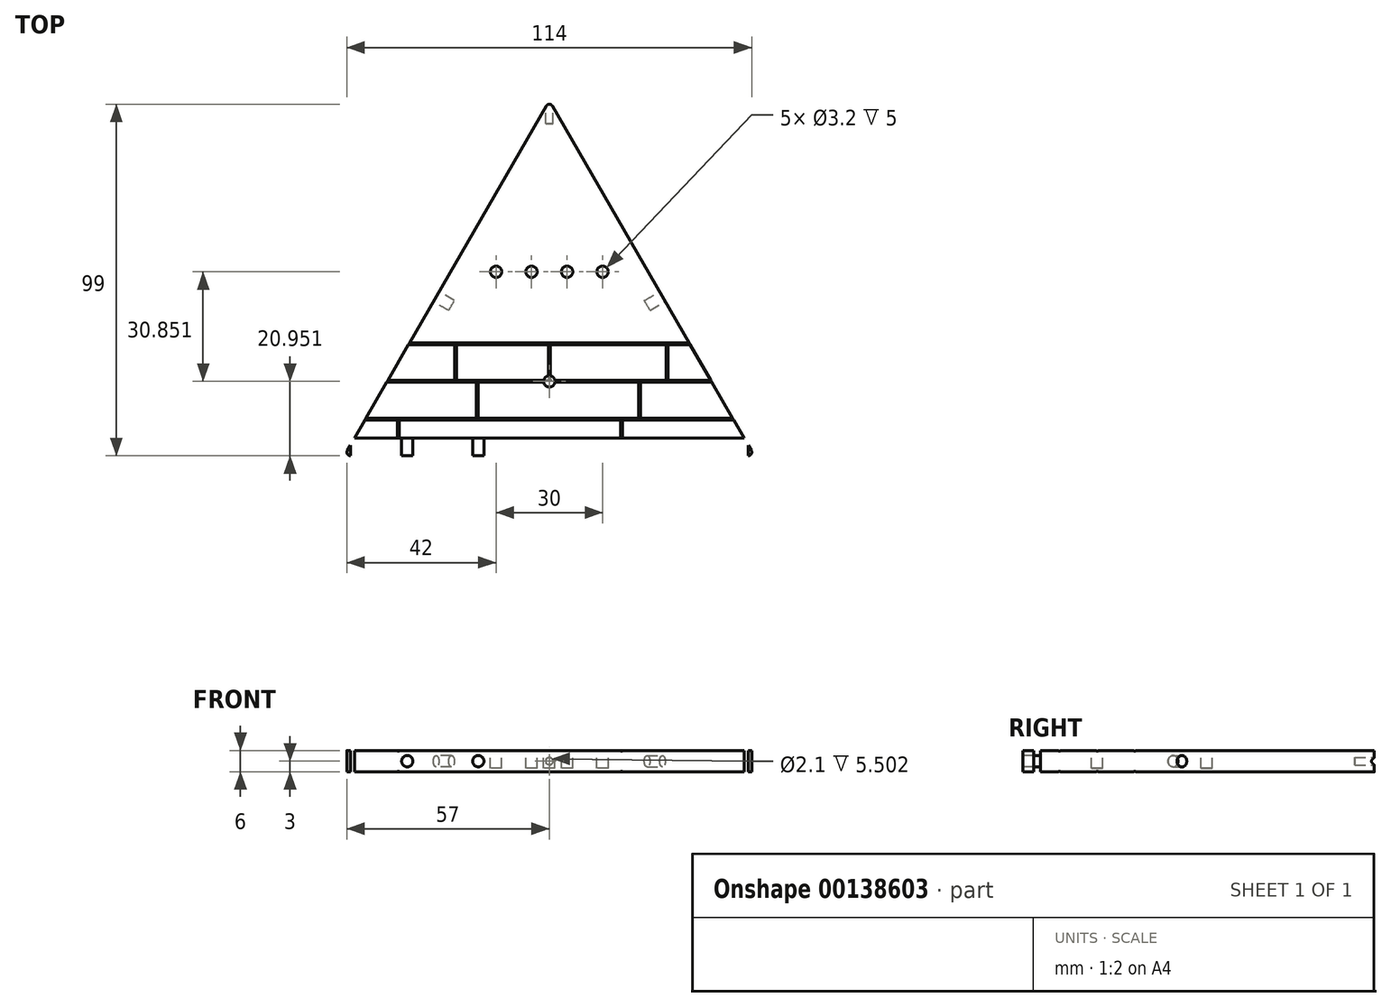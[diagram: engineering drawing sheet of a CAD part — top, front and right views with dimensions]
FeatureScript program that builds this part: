
annotation { "Feature Type Name" : "Feature", "Feature Type Description" : "" }
export const myFeature = defineFeature(function(context is Context, id is Id, definition is map)
    precondition{}
    {
        {
            assignVariable(context, id + "F0", {"name" : "mortar_depth", "anyValue" : 0.15 * mm});
        }
        {
            assignVariable(context, id + "F1", {"name" : "pinhole_depth", "anyValue" : 5 * mm});
        }
        {
            var Q0;
            Q0=qCreatedBy(makeId("Top.planeOp"),FACE);
            var sketch = newSketch(context, id + "F2", { "sketchPlane" : qUnion([Q0])});
            skLineSegment(sketch, "E0", {"start": v(-0.87, 98.5) * mm, "end": v(-56.87, 1.5) * mm});
            skLineSegment(sketch, "E1", {"start": v(-56, 0) * mm, "end": v(56, 0) * mm});
            skLineSegment(sketch, "E2", {"start": v(56.87, 1.5) * mm, "end": v(0.87, 98.5) * mm});
            skPoint(sketch, "E3.visualSharp", {"position": v(0, 100) * mm});
            skArc(sketch, "E3.filletArc", {"start": v(0.87, 98.5) * mm, "mid": v(0, 99) * mm, "end": v(-0.87, 98.5) * mm});
            skPoint(sketch, "E4.visualSharp", {"position": v(-57.74, 0) * mm});
            skArc(sketch, "E4.filletArc", {"start": v(-56.87, 1.5) * mm, "mid": v(-56.87, 0.5) * mm, "end": v(-56, 0) * mm});
            skPoint(sketch, "E5.visualSharp", {"position": v(57.74, 0) * mm});
            skArc(sketch, "E5.filletArc", {"start": v(56, 0) * mm, "mid": v(56.87, 0.5) * mm, "end": v(56.87, 1.5) * mm});
            skLineSegment(sketch, "E6", {"start": v(0, 100) * mm, "end": v(0, 0) * mm, "construction": true});
            skSolve(sketch);
        }
        {
            var Q0;
            Q0=makeQuery(id+"F2.imprint","IMPRINT",FACE,{"disambiguationData":[TD([[makeQuery(id+"F2.imprint","IMPRINT",EDGE,{"derivedFrom":sQuery(id+"F2.wireOp",EDGE,"E0")}),1.0]])]});
            extrude(context, id + "F3", {"entities" : qUnion([Q0]), "depth" : 6 * mm});
        }
        {
            var Q0;
            Q0=makeQuery(id+"F3.opExtrude","CAP_FACE",FACE,{"disambiguationData":[OSD([sQuery(id+"F2.wireOp",EDGE,"E0"),sQuery(id+"F2.wireOp",EDGE,"E1"),sQuery(id+"F2.wireOp",EDGE,"E2")])],"isStart":false});
            var sketch = newSketch(context, id + "F4", { "sketchPlane" : qUnion([Q0])});
            skLineSegment(sketch, "E7", {"start": v(39.37, 31.8) * mm, "end": v(-39.37, 31.8) * mm});
            skLineSegment(sketch, "E8.0", {"start": v(-0.87, 98.5) * mm, "end": v(-0.87, 98.5) * mm});
            skLineSegment(sketch, "E8.1", {"start": v(56.87, 1.5) * mm, "end": v(0, 100) * mm});
            skLineSegment(sketch, "E8.2", {"start": v(-57.74, 0) * mm, "end": v(57.74, 0) * mm});
            skLineSegment(sketch, "E9", {"start": v(19.08, 31.8) * mm, "end": v(19.08, 21.2) * mm, "construction": true});
            skLineSegment(sketch, "E10", {"start": v(19.08, 21.2) * mm, "end": v(19.08, 10.6) * mm, "construction": true});
            skLineSegment(sketch, "E11", {"start": v(19.08, 10.6) * mm, "end": v(19.08, 0) * mm, "construction": true});
            skLineSegment(sketch, "E12", {"start": v(45.5, 21.2) * mm, "end": v(33.45, 21.2) * mm});
            skLineSegment(sketch, "E13", {"start": v(51.61, 10.6) * mm, "end": v(25.67, 10.6) * mm});
            skLineSegment(sketch, "E14", {"start": v(-0.24, 31.3) * mm, "end": v(-0.24, 21.2) * mm});
            skLineSegment(sketch, "E15", {"start": v(-26.13, 31.3) * mm, "end": v(-26.13, 21.2) * mm});
            skLineSegment(sketch, "E16", {"start": v(33.45, 31.3) * mm, "end": v(33.45, 21.2) * mm});
            skLineSegment(sketch, "E17", {"start": v(-19.99, 20.7) * mm, "end": v(-19.99, 10.6) * mm});
            skLineSegment(sketch, "E18", {"start": v(25.67, 20.7) * mm, "end": v(25.67, 10.6) * mm});
            skLineSegment(sketch, "E19", {"start": v(-42.79, 10.1) * mm, "end": v(-42.79, 0) * mm});
            skLineSegment(sketch, "E20", {"start": v(20.12, 10.1) * mm, "end": v(20.12, 0) * mm});
            skLineSegment(sketch, "E21.0", {"start": v(39.66, 31.3) * mm, "end": v(33.45, 31.3) * mm});
            skLineSegment(sketch, "E22.0", {"start": v(45.78, 20.7) * mm, "end": v(25.67, 20.7) * mm});
            skLineSegment(sketch, "E23.0", {"start": v(51.9, 10.1) * mm, "end": v(20.62, 10.1) * mm});
            skLineSegment(sketch, "E24.0", {"start": v(-26.63, 31.3) * mm, "end": v(-26.63, 21.2) * mm});
            skLineSegment(sketch, "E25.0", {"start": v(0.26, 31.3) * mm, "end": v(0.26, 21.2) * mm});
            skLineSegment(sketch, "E26.0", {"start": v(32.95, 31.3) * mm, "end": v(32.95, 21.2) * mm});
            skLineSegment(sketch, "E27.0", {"start": v(-20.49, 20.7) * mm, "end": v(-20.49, 10.6) * mm});
            skLineSegment(sketch, "E28.0", {"start": v(25.17, 20.7) * mm, "end": v(25.17, 10.6) * mm});
            skLineSegment(sketch, "E29.0", {"start": v(-42.29, 10.1) * mm, "end": v(-42.29, 0) * mm});
            skLineSegment(sketch, "E30.0", {"start": v(20.62, 10.1) * mm, "end": v(20.62, 0) * mm});
            skLineSegment(sketch, "E31.trimOffspring", {"start": v(-26.63, 31.3) * mm, "end": v(-39.66, 31.3) * mm});
            skLineSegment(sketch, "E32.trimOffspring", {"start": v(-26.63, 21.2) * mm, "end": v(-45.5, 21.2) * mm});
            skLineSegment(sketch, "E33.trimOffspring", {"start": v(-0.24, 31.3) * mm, "end": v(-26.13, 31.3) * mm});
            skLineSegment(sketch, "E34.trimOffspring", {"start": v(32.95, 31.3) * mm, "end": v(0.26, 31.3) * mm});
            skLineSegment(sketch, "E35.trimOffspring", {"start": v(32.95, 21.2) * mm, "end": v(0.26, 21.2) * mm});
            skLineSegment(sketch, "E36.trimOffspring", {"start": v(25.17, 20.7) * mm, "end": v(-19.99, 20.7) * mm});
            skLineSegment(sketch, "E37.trimOffspring", {"start": v(-0.24, 21.2) * mm, "end": v(-26.13, 21.2) * mm});
            skLineSegment(sketch, "E38.trimOffspring", {"start": v(-20.49, 20.7) * mm, "end": v(-45.78, 20.7) * mm});
            skLineSegment(sketch, "E39.trimOffspring", {"start": v(-42.79, 10.1) * mm, "end": v(-51.9, 10.1) * mm});
            skLineSegment(sketch, "E40.trimOffspring", {"start": v(20.12, 10.1) * mm, "end": v(-42.29, 10.1) * mm});
            skLineSegment(sketch, "E41.trimOffspring", {"start": v(-20.49, 10.6) * mm, "end": v(-51.61, 10.6) * mm});
            skLineSegment(sketch, "E42.trimOffspring", {"start": v(25.17, 10.6) * mm, "end": v(-19.99, 10.6) * mm});
            skLineSegment(sketch, "E43.0", {"start": v(0, 100) * mm, "end": v(0, 0) * mm});
            skSolve(sketch);
        }
        {
            var Q0;
            {var subQ15=sQuery(id+"F4.wireOp",EDGE,"E7");Q0=makeQuery(id+"F4.imprint","IMPRINT",FACE,{"disambiguationData":[TD([[makeQuery(id+"F4.imprint","IMPRINT",EDGE,{"derivedFrom":subQ15}),1.0]])]});}
            extrude(context, id + "F5", {"entities" : qUnion([Q0]), "operationType" : NewBodyOperationType.REMOVE, "oppositeDirection" : true, "depth" : getVariable(context, 'mortar_depth')});
        }
        {
            var Q0;
            Q0=makeQuery(id+"F2.imprint","IMPRINT",FACE,{"disambiguationData":[TD([[makeQuery(id+"F2.imprint","IMPRINT",EDGE,{"derivedFrom":sQuery(id+"F2.wireOp",EDGE,"E0")}),1.0]])]});
            var sketch = newSketch(context, id + "F6", { "sketchPlane" : qUnion([Q0])});
            skLineSegment(sketch, "E44.0", {"start": v(-42.79, 10.1) * mm, "end": v(-42.79, 0) * mm});
            skLineSegment(sketch, "E45.0", {"start": v(-42.29, 10.1) * mm, "end": v(-42.29, 0) * mm});
            skLineSegment(sketch, "E46.0", {"start": v(20.12, 10.1) * mm, "end": v(-42.29, 10.1) * mm});
            skLineSegment(sketch, "E47.0", {"start": v(-20.49, 10.6) * mm, "end": v(-51.61, 10.6) * mm});
            skLineSegment(sketch, "E48.0", {"start": v(-42.79, 10.1) * mm, "end": v(-51.9, 10.1) * mm});
            skLineSegment(sketch, "E49.0", {"start": v(25.17, 10.6) * mm, "end": v(-19.99, 10.6) * mm});
            skLineSegment(sketch, "E50.0", {"start": v(-19.99, 20.7) * mm, "end": v(-19.99, 10.6) * mm});
            skLineSegment(sketch, "E51.0", {"start": v(-20.49, 20.7) * mm, "end": v(-20.49, 10.6) * mm});
            skLineSegment(sketch, "E52.0", {"start": v(20.12, 10.1) * mm, "end": v(20.12, 0) * mm});
            skLineSegment(sketch, "E53.0", {"start": v(20.62, 10.1) * mm, "end": v(20.62, 0) * mm});
            skLineSegment(sketch, "E54.0", {"start": v(51.9, 10.1) * mm, "end": v(20.62, 10.1) * mm});
            skLineSegment(sketch, "E55.0", {"start": v(51.61, 10.6) * mm, "end": v(25.67, 10.6) * mm});
            skLineSegment(sketch, "E56.0", {"start": v(25.17, 20.7) * mm, "end": v(25.17, 10.6) * mm});
            skLineSegment(sketch, "E57.0", {"start": v(25.67, 20.7) * mm, "end": v(25.67, 10.6) * mm});
            skLineSegment(sketch, "E58.0", {"start": v(45.78, 20.7) * mm, "end": v(25.67, 20.7) * mm});
            skLineSegment(sketch, "E59.0", {"start": v(45.5, 21.2) * mm, "end": v(33.45, 21.2) * mm});
            skLineSegment(sketch, "E60.0", {"start": v(33.45, 31.3) * mm, "end": v(33.45, 21.2) * mm});
            skLineSegment(sketch, "E61.0", {"start": v(39.66, 31.3) * mm, "end": v(33.45, 31.3) * mm});
            skLineSegment(sketch, "E62.0", {"start": v(39.37, 31.8) * mm, "end": v(-39.37, 31.8) * mm});
            skLineSegment(sketch, "E63.0", {"start": v(32.95, 31.3) * mm, "end": v(32.95, 21.2) * mm});
            skLineSegment(sketch, "E64.0", {"start": v(32.95, 31.3) * mm, "end": v(0.26, 31.3) * mm});
            skLineSegment(sketch, "E65.0", {"start": v(32.95, 21.2) * mm, "end": v(0.26, 21.2) * mm});
            skLineSegment(sketch, "E66.0", {"start": v(25.17, 20.7) * mm, "end": v(-19.99, 20.7) * mm});
            skLineSegment(sketch, "E67.0", {"start": v(0.26, 31.3) * mm, "end": v(0.26, 21.2) * mm});
            skLineSegment(sketch, "E68.0", {"start": v(-0.24, 31.3) * mm, "end": v(-0.24, 21.2) * mm});
            skLineSegment(sketch, "E69.0", {"start": v(-0.24, 31.3) * mm, "end": v(-26.13, 31.3) * mm});
            skLineSegment(sketch, "E70.0", {"start": v(-0.24, 21.2) * mm, "end": v(-26.13, 21.2) * mm});
            skLineSegment(sketch, "E71.0", {"start": v(-20.49, 20.7) * mm, "end": v(-45.78, 20.7) * mm});
            skLineSegment(sketch, "E72.0", {"start": v(-26.63, 31.3) * mm, "end": v(-26.63, 21.2) * mm});
            skLineSegment(sketch, "E73.0", {"start": v(-26.13, 31.3) * mm, "end": v(-26.13, 21.2) * mm});
            skLineSegment(sketch, "E74.0", {"start": v(-26.63, 31.3) * mm, "end": v(-39.66, 31.3) * mm});
            skLineSegment(sketch, "E75.0", {"start": v(-26.63, 21.2) * mm, "end": v(-45.5, 21.2) * mm});
            skLineSegment(sketch, "E76.0", {"start": v(-56, 0) * mm, "end": v(56, 0) * mm});
            skLineSegment(sketch, "E77.0", {"start": v(56.87, 1.5) * mm, "end": v(0.87, 98.5) * mm});
            skLineSegment(sketch, "E78.0", {"start": v(-0.87, 98.5) * mm, "end": v(-56.87, 1.5) * mm});
            skSolve(sketch);
        }
        {
            var Q0;
            {var subQ2=sQuery(id+"F6.wireOp",EDGE,"E44.0");Q0=makeQuery(id+"F6.imprint","IMPRINT",FACE,{"disambiguationData":[TD([[makeQuery(id+"F6.imprint","IMPRINT",EDGE,{"derivedFrom":subQ2}),1.0]])]});}
            extrude(context, id + "F7", {"entities" : qUnion([Q0]), "operationType" : NewBodyOperationType.REMOVE, "depth" : getVariable(context, 'mortar_depth')});
        }
        {
            var Q0;
            {var subQ0=sQuery(id+"F2.wireOp",EDGE,"E0");var subQ1=sQuery(id+"F2.wireOp",EDGE,"E2");Q0=makeQuery(id+"F5.boolean.opBoolean","SPLIT",FACE,{"disambiguationData":[TD([makeQuery(id+"F5.opExtrude","SWEPT_FACE",FACE,{"disambiguationData":[OSD([sQuery(id+"F4.wireOp",EDGE,"E7")])]})])],"derivedFrom":makeQuery(id+"F3.opExtrude","CAP_FACE",FACE,{"disambiguationData":[OSD([subQ0,sQuery(id+"F2.wireOp",EDGE,"E1"),subQ1])],"isStart":false})});}
            var sketch = newSketch(context, id + "F8", { "sketchPlane" : qUnion([Q0])});
            skLineSegment(sketch, "E79.0", {"start": v(-1.57, 21.2) * mm, "end": v(-26.13, 21.2) * mm});
            skLineSegment(sketch, "E80.0", {"start": v(-0.24, 31.3) * mm, "end": v(-0.24, 22.53) * mm});
            skLineSegment(sketch, "E81.0", {"start": v(0.26, 31.3) * mm, "end": v(0.26, 22.53) * mm});
            skLineSegment(sketch, "E82.0", {"start": v(32.95, 21.2) * mm, "end": v(1.6, 21.2) * mm});
            skLineSegment(sketch, "E83.0", {"start": v(25.17, 20.7) * mm, "end": v(1.6, 20.7) * mm});
            skLineSegment(sketch, "E84", {"start": v(-0.24, 21.2) * mm, "end": v(0.26, 21.2) * mm, "construction": true});
            skLineSegment(sketch, "E85", {"start": v(0.26, 21.2) * mm, "end": v(0.26, 20.7) * mm, "construction": true});
            skLineSegment(sketch, "E86", {"start": v(0.01, 21.2) * mm, "end": v(0.01, 20.95) * mm, "construction": true});
            skPoint(sketch, "E86.endSnap0", {"position": v(0.26, 20.95) * mm});
            skCircle(sketch, "E87", {"center": v(0.01, 20.95) * mm, "radius": 1.6 * mm});
            skLineSegment(sketch, "E88.trimOffspring", {"start": v(-1.57, 20.7) * mm, "end": v(-19.99, 20.7) * mm});
            skLineSegment(sketch, "E89.0", {"start": v(-0.87, 98.5) * mm, "end": v(-39.37, 31.8) * mm, "construction": true});
            skLineSegment(sketch, "E90.0", {"start": v(39.37, 31.8) * mm, "end": v(0.87, 98.5) * mm, "construction": true});
            skLineSegment(sketch, "E91.0", {"start": v(39.37, 31.8) * mm, "end": v(-39.37, 31.8) * mm, "construction": true});
            skLineSegment(sketch, "E92", {"start": v(0, 51.8) * mm, "end": v(0, 31.8) * mm, "construction": true});
            skLineSegment(sketch, "E93", {"start": v(0, 51.8) * mm, "end": v(5, 51.8) * mm, "construction": true});
            skLineSegment(sketch, "E94", {"start": v(0, 51.8) * mm, "end": v(-5, 51.8) * mm, "construction": true});
            skCircle(sketch, "E95", {"center": v(5, 51.8) * mm, "radius": 1.6 * mm});
            skCircle(sketch, "E96", {"center": v(-5, 51.8) * mm, "radius": 1.6 * mm});
            skLineSegment(sketch, "E97", {"start": v(0, 51.8) * mm, "end": v(15, 51.8) * mm, "construction": true});
            skLineSegment(sketch, "E98", {"start": v(0, 51.8) * mm, "end": v(-15, 51.8) * mm, "construction": true});
            skCircle(sketch, "E99", {"center": v(15, 51.8) * mm, "radius": 1.6 * mm});
            skCircle(sketch, "E100", {"center": v(-15, 51.8) * mm, "radius": 1.6 * mm});
            skPoint(sketch, "E101.orphan", {"position": v(0, 65.67) * mm});
            skSolve(sketch);
        }
        {
            var Q0;
            {var subQ0=sQuery(id+"F8.wireOp",EDGE,"E87");var subQ4=makeQuery(id+"F8.imprint","IMPRINT",VERTEX,{"disambiguationData":[OD(2.0)],"derivedFrom":subQ0});Q0=makeQuery(id+"F8.imprint","IMPRINT",FACE,{"disambiguationData":[TD([[makeQuery(id+"F8.imprint","IMPRINT",EDGE,{"disambiguationData":[TD([[subQ4,1.0]])],"derivedFrom":subQ0}),1.0]])]});}
            var Q1;
            Q1=makeQuery(id+"F8.imprint","IMPRINT",FACE,{"disambiguationData":[TD([[makeQuery(id+"F8.imprint","IMPRINT",EDGE,{"derivedFrom":sQuery(id+"F8.wireOp",EDGE,"E99")}),1.0]])]});
            var Q2;
            Q2=makeQuery(id+"F8.imprint","IMPRINT",FACE,{"disambiguationData":[TD([[makeQuery(id+"F8.imprint","IMPRINT",EDGE,{"derivedFrom":sQuery(id+"F8.wireOp",EDGE,"E95")}),1.0]])]});
            var Q3;
            Q3=makeQuery(id+"F8.imprint","IMPRINT",FACE,{"disambiguationData":[TD([[makeQuery(id+"F8.imprint","IMPRINT",EDGE,{"derivedFrom":sQuery(id+"F8.wireOp",EDGE,"E96")}),1.0]])]});
            var Q4;
            Q4=makeQuery(id+"F8.imprint","IMPRINT",FACE,{"disambiguationData":[TD([[makeQuery(id+"F8.imprint","IMPRINT",EDGE,{"derivedFrom":sQuery(id+"F8.wireOp",EDGE,"E100")}),1.0]])]});
            extrude(context, id + "F9", {"entities" : qUnion([Q0, Q1, Q2, Q3, Q4]), "operationType" : NewBodyOperationType.REMOVE, "oppositeDirection" : true, "depth" : getVariable(context, 'pinhole_depth')});
        }
        {
            var Q0;
            Q0=makeQuery(id+"F3.opExtrude","CAP_VERTEX",VERTEX,{"disambiguationData":[OSD([sQuery(id+"F2.wireOp",EDGE,"E2"),sQuery(id+"F2.wireOp",EDGE,"E3.filletArc")])],"isStart":false});
            var Q1;
            Q1=makeQuery(id+"F3.opExtrude","CAP_VERTEX",VERTEX,{"disambiguationData":[OSD([sQuery(id+"F2.wireOp",EDGE,"E2"),sQuery(id+"F2.wireOp",EDGE,"E3.filletArc")])],"isStart":true});
            var Q2;
            Q2=makeQuery(id+"F3.opExtrude","CAP_VERTEX",VERTEX,{"disambiguationData":[OSD([sQuery(id+"F2.wireOp",EDGE,"E0"),sQuery(id+"F2.wireOp",EDGE,"E3.filletArc")])],"isStart":true});
            cPlane(context, id + "F10", {"entities" : qUnion([Q0, Q1, Q2]), "cplaneType" : CPlaneType.THREE_POINT, "offset" : 25.4 * mm, "width" : 152.4 * mm, "height" : 152.4 * mm});
        }
        {
            var Q0;
            Q0=qCreatedBy(id+"F10.planeOp",FACE);
            var sketch = newSketch(context, id + "F11", { "sketchPlane" : qUnion([Q0])});
            skLineSegment(sketch, "E102.0", {"start": v(-0.87, 6) * mm, "end": v(-39.37, 6) * mm, "construction": true});
            skLineSegment(sketch, "E103.0", {"start": v(39.37, 6) * mm, "end": v(0.87, 6) * mm, "construction": true});
            skLineSegment(sketch, "E104.0", {"start": v(0.87, 6) * mm, "end": v(-0.87, 6) * mm, "construction": true});
            skLineSegment(sketch, "E105.0", {"start": v(56.87, 0) * mm, "end": v(51.9, 0) * mm, "construction": true});
            skLineSegment(sketch, "E106.0", {"start": v(51.9, 0) * mm, "end": v(-0.87, 0) * mm, "construction": true});
            skLineSegment(sketch, "E107.0", {"start": v(-0.87, 0) * mm, "end": v(-39.37, 0) * mm, "construction": true});
            skLineSegment(sketch, "E108.0", {"start": v(-0.87, 6) * mm, "end": v(-0.87, 0) * mm, "construction": true});
            skLineSegment(sketch, "E109.0", {"start": v(0.87, 6) * mm, "end": v(0.87, 0) * mm, "construction": true});
            skLineSegment(sketch, "E110", {"start": v(0, 6) * mm, "end": v(0, 0) * mm, "construction": true});
            skCircle(sketch, "E111", {"center": v(0, 3) * mm, "radius": 1.05 * mm});
            skSolve(sketch);
        }
        {
            var Q0;
            Q0 = qSketchRegion(id + "F11", true);
            var Q1;
            Q1=sQuery(id+"F11.wireOp",EDGE,"E111");
            extrude(context, id + "F12", {"entities" : qUnion([Q0]), "operationType" : NewBodyOperationType.REMOVE, "surfaceEntities" : qUnion([Q1]), "depth" : getVariable(context, 'pinhole_depth'), "hasSecondDirection" : true, "secondDirectionBound" : SecondDirectionBoundingType.THROUGH_ALL, "secondDirectionOppositeDirection" : true, "secondDirectionDepth" : 25.4 * mm});
        }
        {
            var Q0;
            Q0=makeQuery(id+"F3.opExtrude","SWEPT_FACE",FACE,{"disambiguationData":[OSD([sQuery(id+"F2.wireOp",EDGE,"E1")])]});
            var sketch = newSketch(context, id + "F13", { "sketchPlane" : qUnion([Q0])});
            skLineSegment(sketch, "E112.0", {"start": v(-42.29, 6) * mm, "end": v(20.12, 6) * mm});
            skLineSegment(sketch, "E113.0.0", {"start": v(-42.29, 5.85) * mm, "end": v(-42.79, 5.85) * mm});
            skLineSegment(sketch, "E113.0.1", {"start": v(-42.79, 5.85) * mm, "end": v(-42.79, 6) * mm});
            skLineSegment(sketch, "E113.0.2", {"start": v(-42.79, 6) * mm, "end": v(-56, 6) * mm});
            skLineSegment(sketch, "E113.0.3", {"start": v(-56, 6) * mm, "end": v(-56, 0) * mm});
            skLineSegment(sketch, "E113.0.4", {"start": v(-56, 0) * mm, "end": v(-42.79, 0) * mm});
            skLineSegment(sketch, "E113.0.5", {"start": v(56, 0) * mm, "end": v(56, 6) * mm});
            skLineSegment(sketch, "E113.0.6", {"start": v(56, 6) * mm, "end": v(20.62, 6) * mm});
            skLineSegment(sketch, "E113.0.7", {"start": v(20.62, 6) * mm, "end": v(20.62, 5.85) * mm});
            skLineSegment(sketch, "E113.0.8", {"start": v(20.62, 5.85) * mm, "end": v(20.12, 5.85) * mm});
            skLineSegment(sketch, "E113.0.9", {"start": v(20.12, 5.85) * mm, "end": v(20.12, 6) * mm});
            skLineSegment(sketch, "E113.0.10", {"start": v(20.12, 6) * mm, "end": v(-42.29, 6) * mm});
            skLineSegment(sketch, "E113.0.11", {"start": v(-42.29, 6) * mm, "end": v(-42.29, 5.85) * mm});
            skLineSegment(sketch, "E114", {"start": v(0, 6) * mm, "end": v(0, 0) * mm, "construction": true});
            skLineSegment(sketch, "E115", {"start": v(0, 3) * mm, "end": v(20, 3) * mm, "construction": true});
            skLineSegment(sketch, "E116", {"start": v(20, 3) * mm, "end": v(40, 3) * mm, "construction": true});
            skCircle(sketch, "E117", {"center": v(20, 3) * mm, "radius": 1.6 * mm});
            skCircle(sketch, "E118", {"center": v(40, 3) * mm, "radius": 1.6 * mm});
            skCircle(sketch, "E119.MirrorC", {"center": v(-20, 3) * mm, "radius": 1.6 * mm});
            skCircle(sketch, "E120.MirrorC", {"center": v(-40, 3) * mm, "radius": 1.6 * mm});
            skSolve(sketch);
        }
        {
            var Q0;
            Q0=makeQuery(id+"F13.imprint","IMPRINT",FACE,{"disambiguationData":[TD([[makeQuery(id+"F13.imprint","IMPRINT",EDGE,{"derivedFrom":sQuery(id+"F13.wireOp",EDGE,"E120.MirrorC")}),-1.0]])]});
            var Q1;
            Q1=makeQuery(id+"F13.imprint","IMPRINT",FACE,{"disambiguationData":[TD([[makeQuery(id+"F13.imprint","IMPRINT",EDGE,{"derivedFrom":sQuery(id+"F13.wireOp",EDGE,"E119.MirrorC")}),-1.0]])]});
            var Q2;
            Q2=makeQuery(id+"F13.imprint","IMPRINT",FACE,{"disambiguationData":[TD([[makeQuery(id+"F13.imprint","IMPRINT",EDGE,{"derivedFrom":sQuery(id+"F13.wireOp",EDGE,"E117")}),1.0]])]});
            var Q3;
            Q3=makeQuery(id+"F13.imprint","IMPRINT",FACE,{"disambiguationData":[TD([[makeQuery(id+"F13.imprint","IMPRINT",EDGE,{"derivedFrom":sQuery(id+"F13.wireOp",EDGE,"E118")}),1.0]])]});
            extrude(context, id + "F14", {"entities" : qUnion([Q0, Q1, Q2, Q3]), "operationType" : NewBodyOperationType.REMOVE, "oppositeDirection" : true, "depth" : getVariable(context, 'pinhole_depth')});
        }
        {
            var Q0;
            Q0=makeQuery(id+"F3.opExtrude","SWEPT_FACE",FACE,{"disambiguationData":[OSD([sQuery(id+"F2.wireOp",EDGE,"E2")])]});
            var sketch = newSketch(context, id + "F15", { "sketchPlane" : qUnion([Q0])});
            skLineSegment(sketch, "E121.0", {"start": v(-27.14, 0) * mm, "end": v(84.87, 0) * mm, "construction": true});
            skLineSegment(sketch, "E122.0", {"start": v(7.85, 6) * mm, "end": v(84.87, 6) * mm, "construction": true});
            skLineSegment(sketch, "E123", {"start": v(22.86, 0) * mm, "end": v(22.86, 6) * mm, "construction": true});
            skCircle(sketch, "E124", {"center": v(22.86, 3) * mm, "radius": 1.6 * mm});
            skLineSegment(sketch, "E125.0", {"start": v(-27.14, 6) * mm, "end": v(-27.14, 0) * mm});
            skSolve(sketch);
        }
        {
            var Q0;
            Q0=makeQuery(id+"F15.imprint","IMPRINT",FACE,{"disambiguationData":[TD([[makeQuery(id+"F15.imprint","IMPRINT",EDGE,{"derivedFrom":sQuery(id+"F15.wireOp",EDGE,"E124")}),1.0]])]});
            var Q1;
            Q1=sQuery(id+"F15.wireOp",EDGE,"E124");
            extrude(context, id + "F16", {"entities" : qUnion([Q0]), "operationType" : NewBodyOperationType.REMOVE, "surfaceEntities" : qUnion([Q1]), "oppositeDirection" : true, "depth" : getVariable(context, 'pinhole_depth')});
        }
        {
            var Q0;
            Q0=makeQuery(id+"F3.opExtrude","SWEPT_FACE",FACE,{"disambiguationData":[OSD([sQuery(id+"F2.wireOp",EDGE,"E0")])]});
            var sketch = newSketch(context, id + "F17", { "sketchPlane" : qUnion([Q0])});
            skLineSegment(sketch, "E126.0", {"start": v(-84.87, 0) * mm, "end": v(27.14, 0) * mm, "construction": true});
            skLineSegment(sketch, "E127.0", {"start": v(-84.87, 6) * mm, "end": v(-7.85, 6) * mm, "construction": true});
            skLineSegment(sketch, "E128.0", {"start": v(27.14, 6) * mm, "end": v(27.14, 0) * mm, "construction": true});
            skLineSegment(sketch, "E129", {"start": v(-22.86, 0) * mm, "end": v(-22.86, 6) * mm, "construction": true});
            skCircle(sketch, "E130", {"center": v(-22.86, 3) * mm, "radius": 1.6 * mm});
            skSolve(sketch);
        }
        {
            var Q0;
            Q0=makeQuery(id+"F17.imprint","IMPRINT",FACE,{"disambiguationData":[TD([[makeQuery(id+"F17.imprint","IMPRINT",EDGE,{"derivedFrom":sQuery(id+"F17.wireOp",EDGE,"E130")}),1.0]])]});
            var Q1;
            Q1=sQuery(id+"F17.wireOp",EDGE,"E130");
            extrude(context, id + "F18", {"entities" : qUnion([Q0]), "operationType" : NewBodyOperationType.REMOVE, "surfaceEntities" : qUnion([Q1]), "oppositeDirection" : true, "depth" : getVariable(context, 'pinhole_depth')});
        }
    });
